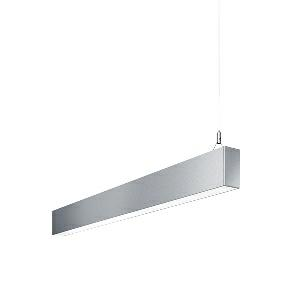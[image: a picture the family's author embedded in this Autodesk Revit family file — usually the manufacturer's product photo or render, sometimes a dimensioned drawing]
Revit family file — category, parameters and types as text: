
# Revit family: idoo_line_-_ilp_4000_830_d_end_00805742_8106
name_source: partatom
category: Lighting Fixtures
units: mm (PartAtom-declared; Revit-internal decimal feet)

## family parameters
Cut with Voids When Loaded = No
Host = Face
Light Source = No
Part Type = Normal
Room Calculation Point = No
Round Connector Dimension = Use Diameter
Shared = No

## types (1)
- IDOO.line - ILP 4000/830/D END (1 x LED, 3750 lm, 3000K)
    Apparent Load = 29 VA
    Approval mark = CE
    CIE Flux Codes = 66 91 98 40 100
    Color Rendering = 80-89
    Color Temperature = 3000K
    Control Gear = Electronic ballast
    Default Elevation = 1800 mm
    Description = ILP 4000/830/D|Suspended luminaire|light source: LED|connected load: 220-240 V, 50/60 Hz|Power consumption: approx. 29 W|standby: approx. 0,15|luminous flux: 3750 lm|luminous efficacy: 129 lm/W|light distribution: Direct/indirect|direct ratio: approx. 40 %|colour temperature: Warm white, ca. 3000 K|color rendering index (CRI): >= 80|chromaticity tolerance:  3 SDCM|System of protection: IP 40|technology: Continuously dimmable|luminaire body|material: Sectional aluminium|colour: Silver|lamp cover: Acrylic (PMMA), Clear|mains lead: 1,0 m With free stranded wires|Fastening: Steel cable 0.3 - 0.7 m|glare control: Prism aperture|luminance(L65): <= 2700 cd/m|unified glare rating(4H 8H): <=  16|special features: DALI Load 1x, TouchDIM - dimming via standard switch, Through-wired, up to 18 m on one mains connection, Flicker-free, Suitable as emergency lighting, Mechanical and electrical connection of the individual modules without tools|
    Frequency = 50 Hz
    Height = 110 mm
    Lamp = 1 x LED
    Lamp Light Flux = 3750 lm
    Lamp count = 1
    Length = 1408 mm
    Luminous efficacy = 129 lm/W
    Manufacturer = Waldmann
    ModVariant = No
    Model = 00805742
    Mounting Place = Ceiling
    Mounting Type = Pendant
    Number of Poles = 1
    OnlyDefault = Yes
    Power Factor = 1
    Product Name = IDOO.line - ILP 4000/830/D END
    Product group = Suspended luminaire
    ProductGroupID = 9
    Protection Class = Protection class I
    Protection Degree = IP 40
    RLX_Detail_Level = 1
    RLX_Emergency_Light_Flux = 0 lm
    RLX_Emergency_Type = 0
    RLX_Emergency_Type_DB = No
    RlxData = <blob elided: 20593 chars, md5=88a7c2be>
    Socket = socket
    Standby Power = 0 W
    System Light Flux = 3750 lm
    System Power = 29 W
    Type Comments = Product without accessories
    Type Image = 113312000-00692600.jpg
    URL = http://relux.com
    VarID = ---
    Voltage = 230 V
    Voltage Range = 220-240 V
    Weight = 0.00 kg
    Width = 60 mm  [stored 0.19685 ft]

note: [stored X ft] marks values corroborated as IEEE doubles in the binary element streams (Revit-internal decimal feet)

## geometry (parser evidence)
native form markers: Blend x4, Sweep x13
no freeform markers — native parametric forms only
